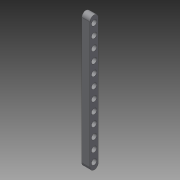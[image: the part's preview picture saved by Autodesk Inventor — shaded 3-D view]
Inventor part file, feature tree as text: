
AUTODESK INVENTOR PART (.ipt)
format: ipt  version: 2015 (Build 190159000, 159)  size: 133,632 bytes
history: native  units: in
note: dims shown in document units (in); Inventor stores cm internally (conversion verified against a paired STEP export)
features: extrude x3, sketch x3
ambient origin geometry x8: Origin, YZ Plane, XZ Plane, XY Plane, X Axis, Y Axis, Z Axis, Center Point
bodies: Solid1 (feature_tree)
feature tree (6):
  extrude  "Extrusion1"  Depth=3.0in
  extrude  "Extrusion2"  Depth=3.0in
  extrude  "Extrusion3"  Depth=3.0in
  sketch  "Sketch1"  dims[d0=72.0in d1=3.0in]
  sketch  "Sketch2"  dims[d2=3.0in d3=0.0in d4=2.0in]
  sketch  "Sketch3"  dims[d5=2.0in d6=2.0in d7=2.0in d8=2.0in d9=2.0in d10=2.0in d11=2.0in d12=2.0in d13=2.0in d14=2.0in d15=2.0in d16=2.0in d17=2.0in d18=2.0in d19=2.0in d20=2.0in d21=5.0in d22=0.0in d23=3.0in d24=0.0in]
